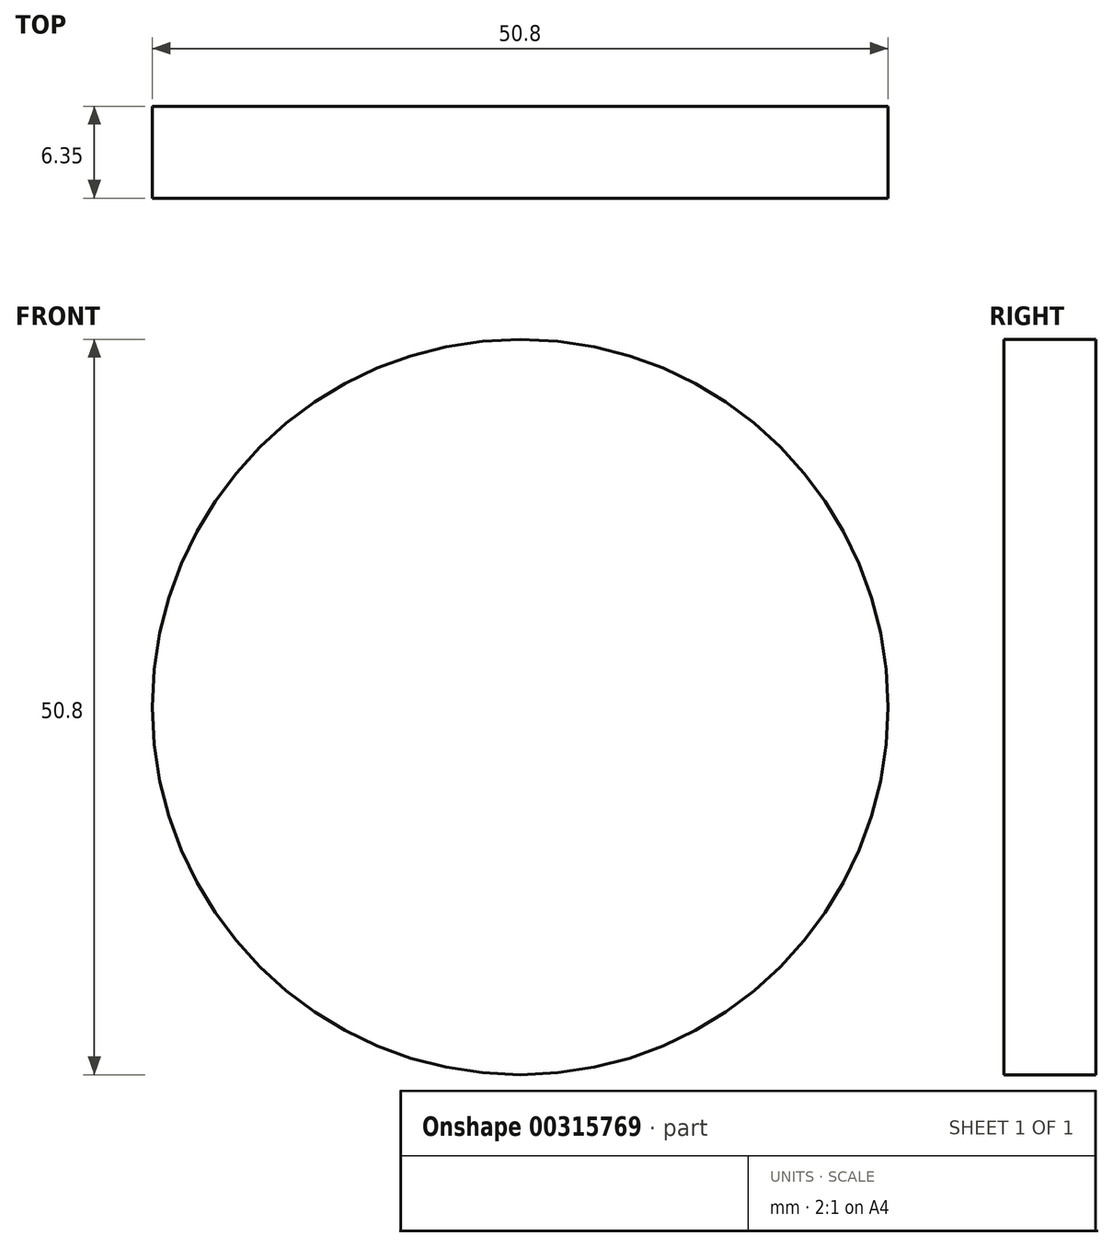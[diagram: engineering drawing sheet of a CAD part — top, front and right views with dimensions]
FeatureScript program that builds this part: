
annotation { "Feature Type Name" : "Feature", "Feature Type Description" : "" }
export const myFeature = defineFeature(function(context is Context, id is Id, definition is map)
    precondition{}
    {
        {
            var Q0;
            Q0=qCreatedBy(makeId("Front.planeOp"),FACE);
            var sketch = newSketch(context, id + "F0", { "sketchPlane" : qUnion([Q0])});
            skCircle(sketch, "E0", {"center": v(0, 0) * mm, "radius": 25.4 * mm});
            skSolve(sketch);
        }
        {
            var Q0;
            Q0=makeQuery(id+"F0.imprint","IMPRINT",FACE,{"disambiguationData":[TD([[makeQuery(id+"F0.imprint","IMPRINT",EDGE,{"derivedFrom":sQuery(id+"F0.wireOp",EDGE,"E0")}),1.0]])]});
            extrude(context, id + "F1", {"entities" : qUnion([Q0]), "depth" : 6.35 * mm});
        }
    });
